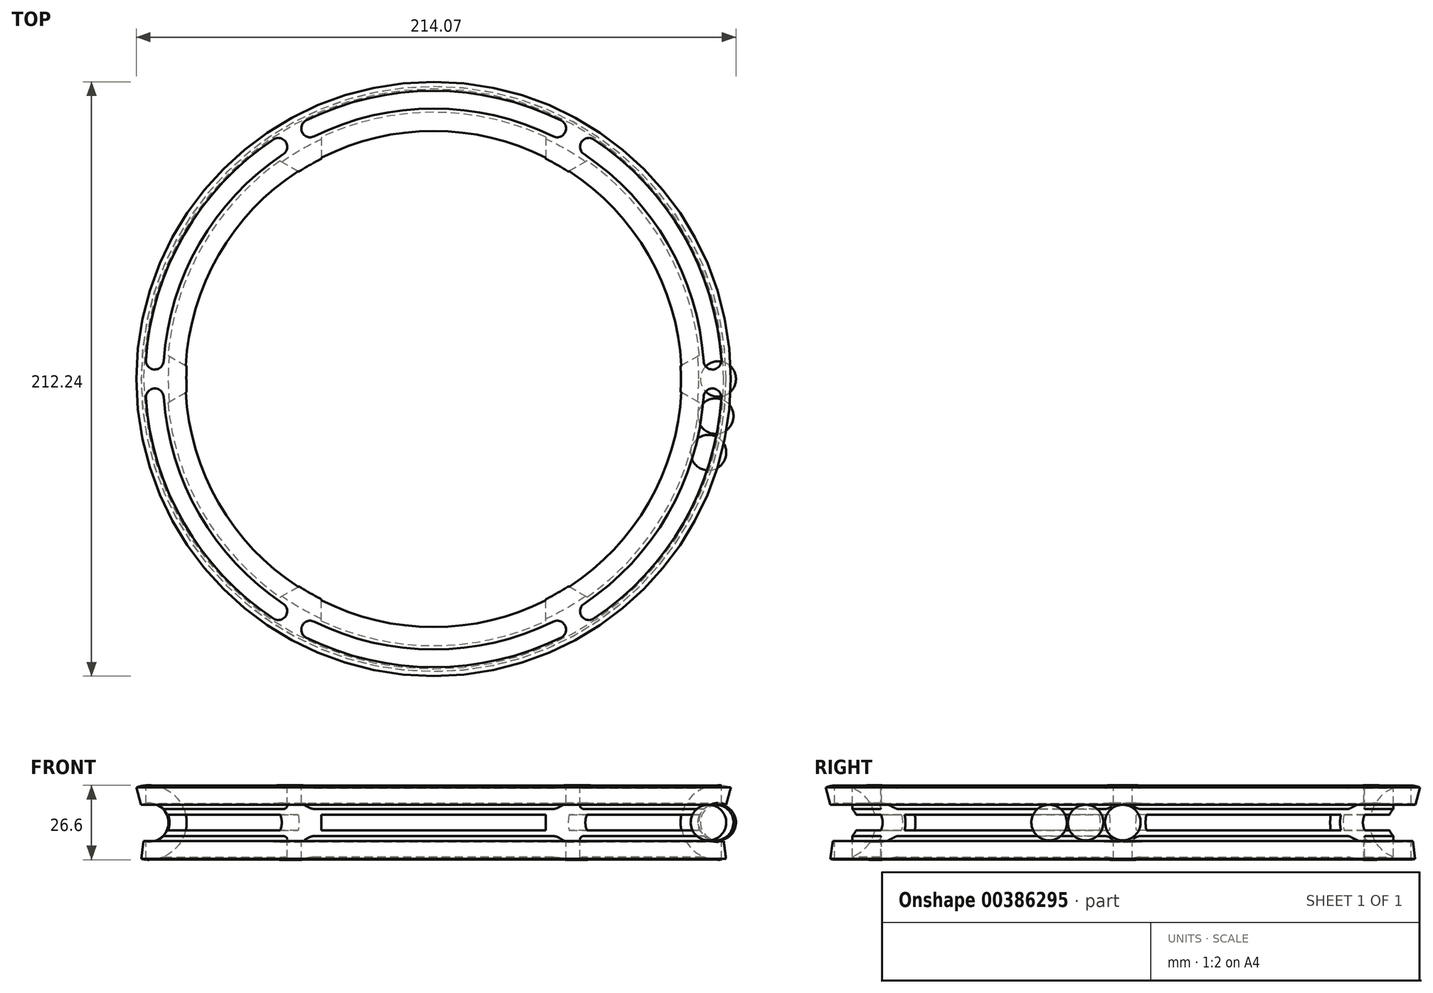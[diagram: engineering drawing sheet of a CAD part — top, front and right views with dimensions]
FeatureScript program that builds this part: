
annotation { "Feature Type Name" : "Feature", "Feature Type Description" : "" }
export const myFeature = defineFeature(function(context is Context, id is Id, definition is map)
    precondition{}
    {
        {
            var Q0;
            Q0=qCreatedBy(makeId("Front.planeOp"),FACE);
            var sketch = newSketch(context, id + "F0", { "sketchPlane" : qUnion([Q0])});
            skArc(sketch, "E0", {"start": v(104.45, 6.34) * mm, "mid": v(94.66, 0.46) * mm, "end": v(103.6, -6.66) * mm});
            skArc(sketch, "E1.0", {"start": v(106.12, 12.5) * mm, "mid": v(88.33, 0.9) * mm, "end": v(104.4, -13) * mm});
            skLineSegment(sketch, "E2", {"start": v(104.45, 6.34) * mm, "end": v(106.12, 12.5) * mm});
            skLineSegment(sketch, "E3", {"start": v(104.4, -13) * mm, "end": v(103.6, -6.66) * mm});
            skLineSegment(sketch, "E4", {"start": v(0, 22.2) * mm, "end": v(0, -13.55) * mm, "construction": true});
            skSolve(sketch);
        }
        {
            var Q0;
            Q0=qSketchRegion(id+"F0",true);
            var Q1;
            Q1=sQuery(id+"F0.wireOp",EDGE,"E4");
            revolve(context, id + "F1", {"entities" : qUnion([Q0]), "axis" : qUnion([Q1]), "revolveType" : RevolveType.FULL});
        }
        {
            var Q0;
            Q0=qCreatedBy(makeId("Right.planeOp"),FACE);
            var sketch = newSketch(context, id + "F2", { "sketchPlane" : qUnion([Q0])});
            skLineSegment(sketch, "E5", {"start": v(0, 23.82) * mm, "end": v(0, -28.67) * mm, "construction": true});
            skSolve(sketch);
        }
        {
            var Q0;
            Q0=qCreatedBy(makeId("Top.planeOp"),FACE);
            var sketch = newSketch(context, id + "F3", { "sketchPlane" : qUnion([Q0])});
            skArc(sketch, "E6.0", {"start": v(45.5, 92.35) * mm, "mid": v(0, 102.95) * mm, "end": v(-45.5, 92.35) * mm});
            skPoint(sketch, "E7", {"position": v(0, 102.95) * mm});
            skPoint(sketch, "E8", {"position": v(45.5, 92.35) * mm});
            skPoint(sketch, "E9", {"position": v(-45.5, 92.35) * mm});
            skArc(sketch, "E10.0", {"start": v(42.69, 86.66) * mm, "mid": v(0, 96.6) * mm, "end": v(-42.69, 86.66) * mm});
            skArc(sketch, "E11", {"start": v(-42.69, 86.66) * mm, "mid": v(-46.94, 88.1) * mm, "end": v(-45.5, 92.35) * mm});
            skArc(sketch, "E12", {"start": v(42.69, 86.66) * mm, "mid": v(46.94, 88.1) * mm, "end": v(45.5, 92.35) * mm});
            skSolve(sketch);
        }
        {
            var Q0;
            Q0=qSketchRegion(id+"F3",true);
            extrude(context, id + "F4", {"entities" : qUnion([Q0]), "operationType" : NewBodyOperationType.REMOVE, "endBound" : BoundingType.THROUGH_ALL, "oppositeDirection" : true, "depth" : 25.4 * mm, "hasSecondDirection" : true, "secondDirectionBound" : SecondDirectionBoundingType.THROUGH_ALL, "secondDirectionOppositeDirection" : false, "secondDirectionDepth" : 25.4 * mm});
        }
        {
            var Q0;
            Q0=makeQuery(id+"F1.opRevolve","SWEPT_BODY",BODY,{"disambiguationData":[OSD([sQuery(id+"F0.wireOp",EDGE,"E0"),sQuery(id+"F0.wireOp",EDGE,"E1.0"),sQuery(id+"F0.wireOp",EDGE,"E2"),sQuery(id+"F0.wireOp",EDGE,"E3")])]});
            var Q1;
            Q1=makeQuery(id+"F4.boolean.opBoolean","COPY",FACE,{"disambiguationData":[OD(1.0)],"derivedFrom":makeQuery(id+"F4.opExtrude","SWEPT_FACE",FACE,{"disambiguationData":[OSD([sQuery(id+"F3.wireOp",EDGE,"E10.0")])]})});
            var Q2;
            Q2=makeQuery(id+"F4.boolean.opBoolean","COPY",FACE,{"disambiguationData":[OD(1.0)],"derivedFrom":makeQuery(id+"F4.opExtrude","SWEPT_FACE",FACE,{"disambiguationData":[OSD([sQuery(id+"F3.wireOp",EDGE,"E11")])]})});
            var Q3;
            Q3=makeQuery(id+"F4.boolean.opBoolean","COPY",FACE,{"disambiguationData":[OD(1.0)],"derivedFrom":makeQuery(id+"F4.opExtrude","SWEPT_FACE",FACE,{"disambiguationData":[OSD([sQuery(id+"F3.wireOp",EDGE,"E6.0")])]})});
            var Q4;
            Q4=makeQuery(id+"F4.boolean.opBoolean","COPY",FACE,{"disambiguationData":[OD(1.0)],"derivedFrom":makeQuery(id+"F4.opExtrude","SWEPT_FACE",FACE,{"disambiguationData":[OSD([sQuery(id+"F3.wireOp",EDGE,"E12")])]})});
            var Q5;
            Q5=makeQuery(id+"F4.boolean.opBoolean","COPY",FACE,{"disambiguationData":[OD(0.0)],"derivedFrom":makeQuery(id+"F4.opExtrude","SWEPT_FACE",FACE,{"disambiguationData":[OSD([sQuery(id+"F3.wireOp",EDGE,"E10.0")])]})});
            var Q6;
            Q6=makeQuery(id+"F4.boolean.opBoolean","COPY",FACE,{"disambiguationData":[OD(0.0)],"derivedFrom":makeQuery(id+"F4.opExtrude","SWEPT_FACE",FACE,{"disambiguationData":[OSD([sQuery(id+"F3.wireOp",EDGE,"E6.0")])]})});
            var Q7;
            Q7=makeQuery(id+"F4.boolean.opBoolean","COPY",FACE,{"disambiguationData":[OD(0.0)],"derivedFrom":makeQuery(id+"F4.opExtrude","SWEPT_FACE",FACE,{"disambiguationData":[OSD([sQuery(id+"F3.wireOp",EDGE,"E12")])]})});
            var Q8;
            Q8=makeQuery(id+"F4.boolean.opBoolean","COPY",FACE,{"disambiguationData":[OD(0.0)],"derivedFrom":makeQuery(id+"F4.opExtrude","SWEPT_FACE",FACE,{"disambiguationData":[OSD([sQuery(id+"F3.wireOp",EDGE,"E11")])]})});
            var Q9;
            Q9=sQuery(id+"F2.wireOp",EDGE,"E5");
            circularPattern(context, id + "F5", {"faces" : qUnion([Q1, Q2, Q3, Q4, Q5, Q6, Q7, Q8]), "axis" : qUnion([Q9]), "angle" : 360 * degree, "instanceCount" : 6, "equalSpace" : true, "patternType" : PatternType.FACE});
        }
        {
            var Q0;
            Q0=qCreatedBy(makeId("Front.planeOp"),FACE);
            var sketch = newSketch(context, id + "F6", { "sketchPlane" : qUnion([Q0])});
            skLineSegment(sketch, "E13", {"start": v(101.6, -6.35) * mm, "end": v(101.6, 6.35) * mm});
            skArc(sketch, "E14", {"start": v(101.6, -6.35) * mm, "mid": v(107.95, 0) * mm, "end": v(101.6, 6.35) * mm});
            skLineSegment(sketch, "E15", {"start": v(101.6, 0) * mm, "end": v(101.6, 17.07) * mm});
            skLineSegment(sketch, "E16", {"start": v(101.6, 17.07) * mm, "end": v(101.6, -14.7) * mm});
            skSolve(sketch);
        }
        {
            var Q0;
            {var subQ1=sQuery(id+"F6.wireOp",EDGE,"E14");Q0=makeQuery(id+"F6.imprint","IMPRINT",FACE,{"disambiguationData":[TD([[makeQuery(id+"F6.imprint","IMPRINT",EDGE,{"derivedFrom":subQ1}),1.0]])]});}
            var Q1;
            Q1=sQuery(id+"F6.wireOp",EDGE,"E16");
            revolve(context, id + "F7", {"entities" : qUnion([Q0]), "axis" : qUnion([Q1]), "revolveType" : RevolveType.FULL});
        }
        {
            var Q0;
            Q0=qCreatedBy(makeId("Front.planeOp"),FACE);
            var sketch = newSketch(context, id + "F8", { "sketchPlane" : qUnion([Q0])});
            skLineSegment(sketch, "E17.rect.bottom", {"start": v(40.1, -2.83) * mm, "end": v(-40.1, -2.83) * mm});
            skLineSegment(sketch, "E17.rect.top", {"start": v(40.1, 2.83) * mm, "end": v(-40.1, 2.83) * mm});
            skLineSegment(sketch, "E17.rect.left", {"start": v(40.1, -2.83) * mm, "end": v(40.1, 2.83) * mm});
            skLineSegment(sketch, "E17.rect.right", {"start": v(-40.1, -2.83) * mm, "end": v(-40.1, 2.83) * mm});
            skPoint(sketch, "E17.rect.middle", {"position": v(0, 0) * mm});
            skSolve(sketch);
        }
        {
            var Q0;
            Q0=qSketchRegion(id+"F8",true);
            extrude(context, id + "F9", {"entities" : qUnion([Q0]), "operationType" : NewBodyOperationType.REMOVE, "endBound" : BoundingType.THROUGH_ALL, "oppositeDirection" : true, "depth" : 25.4 * mm});
        }
        {
            var Q0;
            Q0=makeQuery(id+"F9.boolean.opBoolean","COPY",FACE,{"derivedFrom":makeQuery(id+"F9.opExtrude","SWEPT_FACE",FACE,{"disambiguationData":[OSD([sQuery(id+"F8.wireOp",EDGE,"E17.rect.bottom")])]})});
            var Q1;
            Q1=makeQuery(id+"F9.boolean.opBoolean","COPY",FACE,{"derivedFrom":makeQuery(id+"F9.opExtrude","SWEPT_FACE",FACE,{"disambiguationData":[OSD([sQuery(id+"F8.wireOp",EDGE,"E17.rect.top")])]})});
            var Q2;
            Q2=makeQuery(id+"F9.boolean.opBoolean","COPY",FACE,{"derivedFrom":makeQuery(id+"F9.opExtrude","SWEPT_FACE",FACE,{"disambiguationData":[OSD([sQuery(id+"F8.wireOp",EDGE,"E17.rect.right")])]})});
            var Q3;
            Q3=makeQuery(id+"F9.boolean.opBoolean","COPY",FACE,{"derivedFrom":makeQuery(id+"F9.opExtrude","SWEPT_FACE",FACE,{"disambiguationData":[OSD([sQuery(id+"F8.wireOp",EDGE,"E17.rect.left")])]})});
            var Q4;
            Q4=sQuery(id+"F2.wireOp",EDGE,"E5");
            circularPattern(context, id + "F10", {"operationType" : NewBodyOperationType.ADD, "faces" : qUnion([Q0, Q1, Q2, Q3]), "axis" : qUnion([Q4]), "angle" : 360 * degree, "instanceCount" : 6, "oppositeDirection" : true, "equalSpace" : true, "patternType" : PatternType.FACE});
        }
        {
            var Q0;
            Q0=makeQuery(id+"F7.opRevolve","SWEPT_BODY",BODY,{"disambiguationData":[OSD([sQuery(id+"F6.wireOp",EDGE,"E14"),sQuery(id+"F6.wireOp",EDGE,"E16")])]});
            var Q1;
            Q1=sQuery(id+"F0.wireOp",EDGE,"E4");
            circularPattern(context, id + "F11", {"entities" : qUnion([Q0]), "axis" : qUnion([Q1]), "angle" : 15 * degree, "instanceCount" : 3, "equalSpace" : true});
        }
    });
